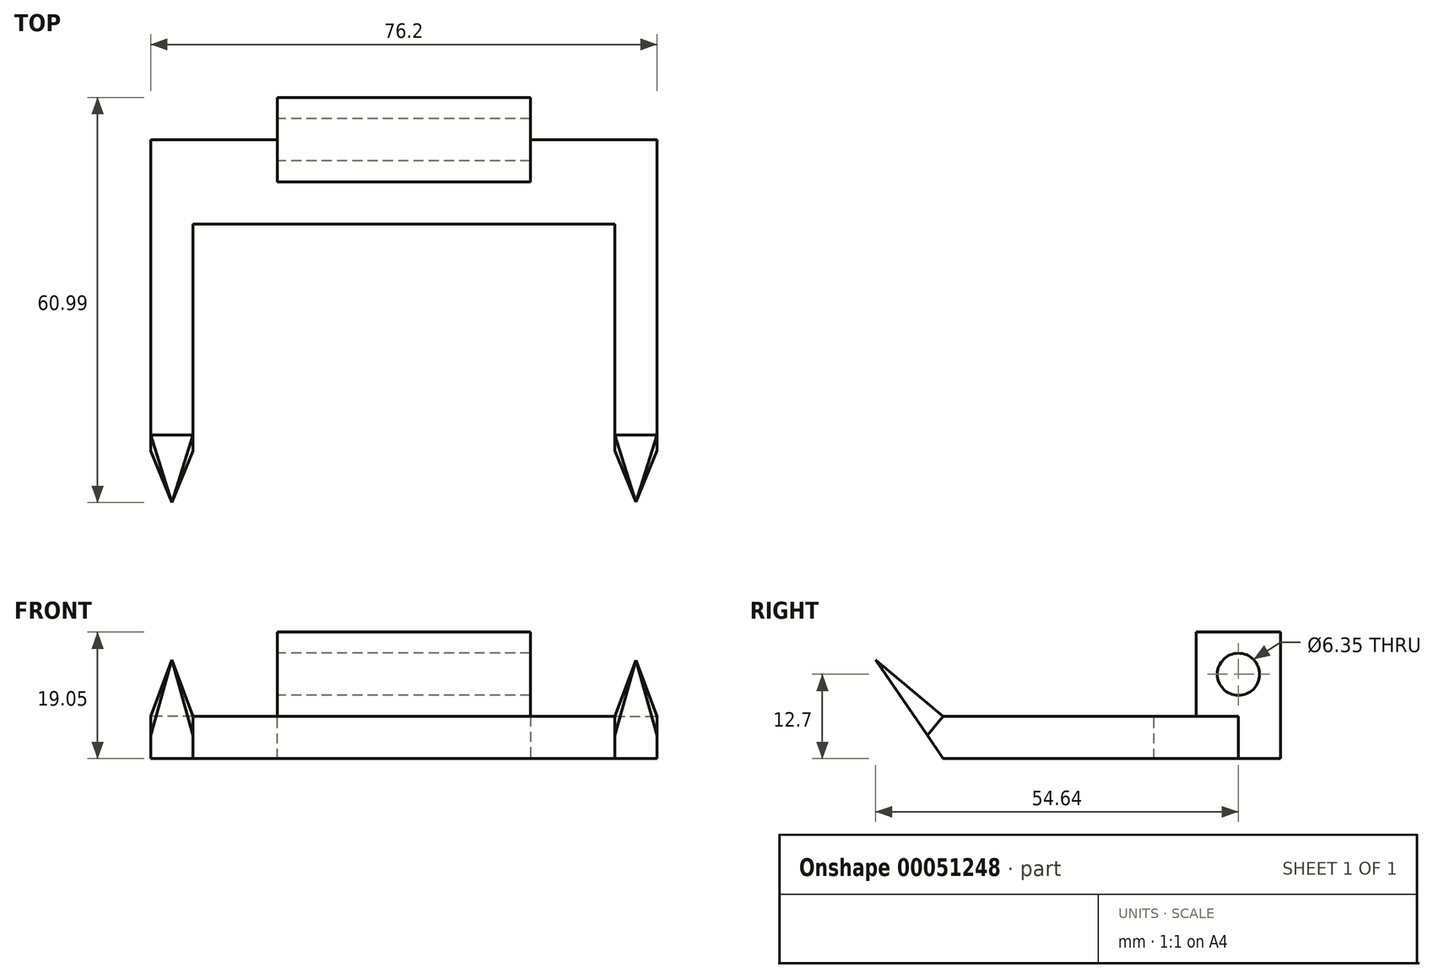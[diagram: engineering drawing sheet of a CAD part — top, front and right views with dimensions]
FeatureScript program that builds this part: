
annotation { "Feature Type Name" : "Feature", "Feature Type Description" : "" }
export const myFeature = defineFeature(function(context is Context, id is Id, definition is map)
    precondition{}
    {
        {
            var Q0;
            Q0=qCreatedBy(makeId("Right.planeOp"),FACE);
            var sketch = newSketch(context, id + "F0", { "sketchPlane" : qUnion([Q0])});
            skLineSegment(sketch, "E0.bottom", {"start": v(0, 0) * mm, "end": v(-12.7, 0) * mm});
            skLineSegment(sketch, "E0.top", {"start": v(0, 19.05) * mm, "end": v(-12.7, 19.05) * mm});
            skLineSegment(sketch, "E0.left", {"start": v(0, 0) * mm, "end": v(0, 19.05) * mm});
            skLineSegment(sketch, "E0.right", {"start": v(-12.7, 0) * mm, "end": v(-12.7, 19.05) * mm});
            skLineSegment(sketch, "E1", {"start": v(-6.35, 19.05) * mm, "end": v(-6.35, 0) * mm, "construction": true});
            skLineSegment(sketch, "E2", {"start": v(-12.7, 12.7) * mm, "end": v(0, 12.7) * mm});
            skCircle(sketch, "E3", {"center": v(-6.35, 12.7) * mm, "radius": 3.18 * mm});
            skSolve(sketch);
        }
        {
            var Q0;
            {var subQ5=sQuery(id+"F0.wireOp",EDGE,"E0.bottom");Q0=makeQuery(id+"F0.imprint","IMPRINT",FACE,{"disambiguationData":[TD([[makeQuery(id+"F0.imprint","IMPRINT",EDGE,{"derivedFrom":subQ5}),-1.0]])]});}
            var Q1;
            {var subQ5=sQuery(id+"F0.wireOp",EDGE,"E0.top");Q1=makeQuery(id+"F0.imprint","IMPRINT",FACE,{"disambiguationData":[TD([[makeQuery(id+"F0.imprint","IMPRINT",EDGE,{"derivedFrom":subQ5}),1.0]])]});}
            extrude(context, id + "F1", {"entities" : qUnion([Q0, Q1]), "depth" : 38.1 * mm});
        }
        {
            var Q0;
            Q0=makeQuery(id+"F1.opExtrude","CAP_FACE",FACE,{"disambiguationData":[OSD([sQuery(id+"F0.wireOp",EDGE,"E0.bottom"),sQuery(id+"F0.wireOp",EDGE,"E0.top"),sQuery(id+"F0.wireOp",EDGE,"E0.left"),sQuery(id+"F0.wireOp",EDGE,"E0.right"),sQuery(id+"F0.wireOp",EDGE,"E3")])],"isStart":true});
            var sketch = newSketch(context, id + "F2", { "sketchPlane" : qUnion([Q0])});
            skLineSegment(sketch, "E4.bottom", {"start": v(6.35, 0) * mm, "end": v(19.05, 0) * mm});
            skLineSegment(sketch, "E4.top", {"start": v(6.35, 6.35) * mm, "end": v(19.05, 6.35) * mm});
            skLineSegment(sketch, "E4.left", {"start": v(6.35, 0) * mm, "end": v(6.35, 6.35) * mm});
            skLineSegment(sketch, "E4.right", {"start": v(19.05, 0) * mm, "end": v(19.05, 6.35) * mm});
            skSolve(sketch);
        }
        {
            var Q0;
            {var subQ3=sQuery(id+"F2.wireOp",EDGE,"E4.left");Q0=makeQuery(id+"F2.imprint","IMPRINT",FACE,{"disambiguationData":[TD([[makeQuery(id+"F2.imprint","IMPRINT",EDGE,{"derivedFrom":subQ3}),-1.0]])]});}
            var Q1;
            {var subQ3=sQuery(id+"F2.wireOp",EDGE,"E4.right");Q1=makeQuery(id+"F2.imprint","IMPRINT",FACE,{"disambiguationData":[TD([[makeQuery(id+"F2.imprint","IMPRINT",EDGE,{"derivedFrom":subQ3}),1.0]])]});}
            extrude(context, id + "F3", {"entities" : qUnion([Q0, Q1]), "operationType" : NewBodyOperationType.ADD, "oppositeDirection" : true, "depth" : 57.15 * mm});
        }
        {
            var Q0;
            Q0 = qSketchRegion(id + "F2", true);
            extrude(context, id + "F4", {"entities" : qUnion([Q0]), "operationType" : NewBodyOperationType.ADD, "depth" : 19.05 * mm});
        }
        {
            var Q0;
            Q0=makeQuery(id+"F4.opExtrude","CAP_FACE",FACE,{"disambiguationData":[OSD([sQuery(id+"F2.wireOp",EDGE,"E4.bottom"),sQuery(id+"F2.wireOp",EDGE,"E4.top"),sQuery(id+"F2.wireOp",EDGE,"E4.left"),sQuery(id+"F2.wireOp",EDGE,"E4.right")])],"isStart":false});
            var sketch = newSketch(context, id + "F5", { "sketchPlane" : qUnion([Q0])});
            skLineSegment(sketch, "E5.bottom", {"start": v(19.05, 6.35) * mm, "end": v(50.8, 6.35) * mm});
            skLineSegment(sketch, "E5.top", {"start": v(19.05, 0) * mm, "end": v(50.8, 0) * mm});
            skLineSegment(sketch, "E5.left", {"start": v(19.05, 6.35) * mm, "end": v(19.05, 0) * mm});
            skLineSegment(sketch, "E5.right", {"start": v(50.8, 6.35) * mm, "end": v(50.8, 0) * mm});
            skLineSegment(sketch, "E6", {"start": v(50.8, 6.35) * mm, "end": v(60.99, 14.9) * mm});
            skLineSegment(sketch, "E7", {"start": v(50.8, 0) * mm, "end": v(60.99, 14.9) * mm});
            skSolve(sketch);
        }
        {
            var Q0;
            Q0=makeQuery(id+"F5.imprint","IMPRINT",FACE,{"disambiguationData":[TD([[makeQuery(id+"F5.imprint","IMPRINT",EDGE,{"derivedFrom":sQuery(id+"F5.wireOp",EDGE,"E5.bottom")}),-1.0]])]});
            var Q1;
            Q1=makeQuery(id+"F5.imprint","IMPRINT",FACE,{"disambiguationData":[TD([[makeQuery(id+"F5.imprint","IMPRINT",EDGE,{"derivedFrom":sQuery(id+"F5.wireOp",EDGE,"E5.right")}),1.0]])]});
            extrude(context, id + "F6", {"entities" : qUnion([Q0, Q1]), "operationType" : NewBodyOperationType.ADD, "oppositeDirection" : true, "depth" : 6.35 * mm});
        }
        {
            var Q0;
            Q0=makeQuery(id+"F3.opExtrude","CAP_FACE",FACE,{"disambiguationData":[OSD([sQuery(id+"F2.wireOp",EDGE,"E4.bottom"),sQuery(id+"F2.wireOp",EDGE,"E4.top"),sQuery(id+"F2.wireOp",EDGE,"E4.left"),sQuery(id+"F2.wireOp",EDGE,"E4.right")])],"isStart":false});
            var sketch = newSketch(context, id + "F7", { "sketchPlane" : qUnion([Q0])});
            skLineSegment(sketch, "E8.bottom", {"start": v(-19.05, 6.35) * mm, "end": v(-50.8, 6.35) * mm});
            skLineSegment(sketch, "E8.top", {"start": v(-19.05, 0) * mm, "end": v(-50.8, 0) * mm});
            skLineSegment(sketch, "E8.left", {"start": v(-19.05, 6.35) * mm, "end": v(-19.05, 0) * mm});
            skLineSegment(sketch, "E8.right", {"start": v(-50.8, 6.35) * mm, "end": v(-50.8, 0) * mm});
            skLineSegment(sketch, "E9", {"start": v(-50.8, 6.35) * mm, "end": v(-60.91, 14.83) * mm});
            skLineSegment(sketch, "E10", {"start": v(-60.91, 14.83) * mm, "end": v(-50.8, 0) * mm});
            skSolve(sketch);
        }
        {
            var Q0;
            Q0=makeQuery(id+"F7.imprint","IMPRINT",FACE,{"disambiguationData":[TD([[makeQuery(id+"F7.imprint","IMPRINT",EDGE,{"derivedFrom":sQuery(id+"F7.wireOp",EDGE,"E8.right")}),-1.0]])]});
            var Q1;
            Q1=makeQuery(id+"F7.imprint","IMPRINT",FACE,{"disambiguationData":[TD([[makeQuery(id+"F7.imprint","IMPRINT",EDGE,{"derivedFrom":sQuery(id+"F7.wireOp",EDGE,"E8.bottom")}),1.0]])]});
            extrude(context, id + "F8", {"entities" : qUnion([Q0, Q1]), "operationType" : NewBodyOperationType.ADD, "oppositeDirection" : true, "depth" : 6.35 * mm});
        }
        {
            var Q0;
            Q0=makeQuery(id+"F6.opExtrude","SWEPT_FACE",FACE,{"disambiguationData":[OSD([sQuery(id+"F5.wireOp",EDGE,"E6")])]});
            var sketch = newSketch(context, id + "F9", { "sketchPlane" : qUnion([Q0])});
            skLineSegment(sketch, "E11", {"start": v(-19.05, -43) * mm, "end": v(-15.87, -56.3) * mm});
            skLineSegment(sketch, "E12", {"start": v(-15.87, -56.3) * mm, "end": v(-12.7, -43) * mm});
            skSolve(sketch);
        }
        {
            var Q0;
            {var subQ0=sQuery(id+"F9.wireOp",EDGE,"E11");Q0=makeQuery(id+"F9.imprint","IMPRINT",FACE,{"disambiguationData":[TD([[makeQuery(id+"F9.imprint","IMPRINT",EDGE,{"derivedFrom":subQ0}),-1.0]])]});}
            var Q1;
            {var subQ0=sQuery(id+"F9.wireOp",EDGE,"E12");Q1=makeQuery(id+"F9.imprint","IMPRINT",FACE,{"disambiguationData":[TD([[makeQuery(id+"F9.imprint","IMPRINT",EDGE,{"derivedFrom":subQ0}),-1.0]])]});}
            extrude(context, id + "F10", {"entities" : qUnion([Q0, Q1]), "operationType" : NewBodyOperationType.REMOVE, "oppositeDirection" : true, "depth" : 25.4 * mm});
        }
        {
            var Q0;
            Q0=makeQuery(id+"F8.opExtrude","SWEPT_FACE",FACE,{"disambiguationData":[OSD([sQuery(id+"F7.wireOp",EDGE,"E9")])]});
            var sketch = newSketch(context, id + "F11", { "sketchPlane" : qUnion([Q0])});
            skLineSegment(sketch, "E13", {"start": v(53.98, -56.2) * mm, "end": v(50.8, -43) * mm});
            skLineSegment(sketch, "E14", {"start": v(57.15, -43) * mm, "end": v(53.97, -56.2) * mm});
            skSolve(sketch);
        }
        {
            var Q0;
            Q0 = qSketchRegion(id + "F11", true);
            var Q1;
            {var subQ0=sQuery(id+"F11.wireOp",EDGE,"E14");Q1=makeQuery(id+"F11.imprint","IMPRINT",FACE,{"disambiguationData":[TD([[makeQuery(id+"F11.imprint","IMPRINT",EDGE,{"derivedFrom":subQ0}),1.0]])]});}
            var Q2;
            {var subQ0=sQuery(id+"F11.wireOp",EDGE,"E13");Q2=makeQuery(id+"F11.imprint","IMPRINT",FACE,{"disambiguationData":[TD([[makeQuery(id+"F11.imprint","IMPRINT",EDGE,{"derivedFrom":subQ0}),1.0]])]});}
            extrude(context, id + "F12", {"entities" : qUnion([Q0, Q1, Q2]), "operationType" : NewBodyOperationType.REMOVE, "oppositeDirection" : true, "depth" : 25.4 * mm});
        }
    });
